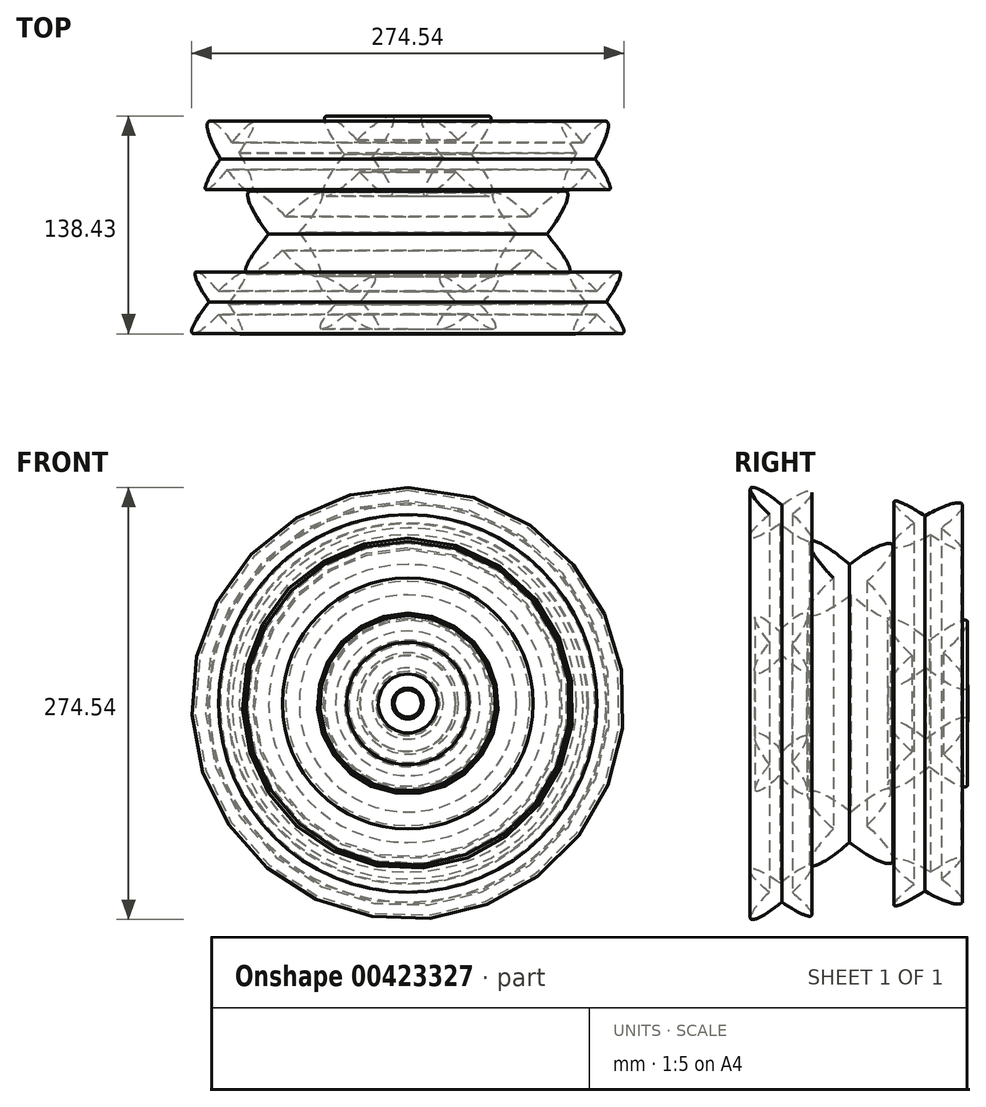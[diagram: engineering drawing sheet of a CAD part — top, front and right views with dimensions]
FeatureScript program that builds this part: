
annotation { "Feature Type Name" : "Feature", "Feature Type Description" : "" }
export const myFeature = defineFeature(function(context is Context, id is Id, definition is map)
    precondition{}
    {
        {
            var Q0;
            Q0=qCreatedBy(makeId("Top.planeOp"),FACE);
            var sketch = newSketch(context, id + "F0", { "sketchPlane" : qUnion([Q0])});
            skEllipticalArc(sketch, "E0", {});
            skEllipticalArc(sketch, "E1", {});
            skEllipticalArc(sketch, "E2.trimOffspring", {});
            skEllipticalArc(sketch, "E3.trimOffspring", {});
            skLineSegment(sketch, "E4", {"start": v(-1.03, 10.72) * mm, "end": v(-9.67, 0.48) * mm});
            skLineSegment(sketch, "E5", {"start": v(1.03, -10.72) * mm, "end": v(9.67, -0.48) * mm});
            skLineSegment(sketch, "E6", {"start": v(-1.03, 10.72) * mm, "end": v(9.67, -0.48) * mm});
            skLineSegment(sketch, "E7", {"start": v(-9.67, 0.48) * mm, "end": v(1.03, -10.72) * mm});
            skEllipse(sketch, "E8", {"center": v(-47.24, 49.23) * mm, "majorRadius": 33.26 * mm, "minorRadius": 7.43 * mm, "majorAxis": v(0.66, -0.75)});
            skEllipse(sketch, "E9", {"center": v(-47.24, 49.23) * mm, "majorRadius": 32.66 * mm, "minorRadius": 6.11 * mm, "majorAxis": v(-0.64, -0.77)});
            skEllipse(sketch, "E10", {"center": v(34.44, 49.23) * mm, "majorRadius": 26.22 * mm, "minorRadius": 3.86 * mm, "majorAxis": v(0.58, -0.81)});
            skEllipse(sketch, "E11", {"center": v(34.44, 49.23) * mm, "majorRadius": 25.72 * mm, "minorRadius": 6.06 * mm, "majorAxis": v(-0.52, -0.85)});
            skEllipse(sketch, "E12", {"center": v(-40.54, -44.04) * mm, "majorRadius": 24.86 * mm, "minorRadius": 5.96 * mm, "majorAxis": v(0.76, 0.65)});
            skEllipse(sketch, "E13", {"center": v(-40.54, -44.04) * mm, "majorRadius": 23.72 * mm, "minorRadius": 4.81 * mm, "majorAxis": v(0.73, -0.68)});
            skEllipse(sketch, "E14", {"center": v(41.45, -44.04) * mm, "majorRadius": 25.5 * mm, "minorRadius": 4.98 * mm, "majorAxis": v(0.66, -0.75)});
            skEllipse(sketch, "E15", {"center": v(41.45, -44.04) * mm, "majorRadius": 24.38 * mm, "minorRadius": 4.5 * mm, "majorAxis": v(-0.6, -0.8)});
            skLineSegment(sketch, "E16", {"start": v(-78.64, 71.48) * mm, "end": v(-78.64, -70.26) * mm});
            const initialGuessF0  = {"E0": [0, 0, -0.6406158775959403, -0.7678615092397738, 0.03473282763399038, 0.007845882429823885, 4.880818733139201, 1.3508733820816232], "E1": [0, 0, 0.6872618986570745, -0.7264097209249565, 0.035036424872981996, 0.006828572059690051, 1.8156771173609703, 4.5113287056147815], "E2.trimOffspring": [0, 0, 0.6872618986570745, -0.7264097209249565, 0.035036424872981996, 0.006828572059690051, 4.957269770950763, 1.3697360520249888], "E3.trimOffspring": [0, 0, -0.6406158775959403, -0.7678615092397738, 0.03473282763399038, 0.007845882429823885, 1.7392260795494074, 4.492466035671416]};
            skSetInitialGuess(sketch, initialGuessF0);
            skSolve(sketch);
        }
        {
            var Q0;
            {var subQ0=sQuery(id+"F0.wireOp",EDGE,"E9");var subQ1=sQuery(id+"F0.wireOp",EDGE,"E8");var subQ2=makeQuery(id+"F0.imprint","INTERSECT",VERTEX,{"disambiguationData":[OD(0.0)],"derivedFrom":[subQ1,subQ0]});Q0=makeQuery(id+"F0.imprint","IMPRINT",FACE,{"disambiguationData":[TD([[makeQuery(id+"F0.imprint","IMPRINT",EDGE,{"disambiguationData":[TD([[subQ2,-1.0]])],"derivedFrom":subQ1}),1.0]])]});}
            var Q1;
            Q1=makeQuery(id+"F0.imprint","IMPRINT",FACE,{"disambiguationData":[TD([[makeQuery(id+"F0.imprint","IMPRINT",EDGE,{"derivedFrom":sQuery(id+"F0.wireOp",EDGE,"E4")}),1.0]])]});
            var Q2;
            {var subQ0=sQuery(id+"F0.wireOp",EDGE,"E15");var subQ1=sQuery(id+"F0.wireOp",EDGE,"E14");var subQ2=makeQuery(id+"F0.imprint","INTERSECT",VERTEX,{"disambiguationData":[OD(2.0)],"derivedFrom":[subQ1,subQ0]});Q2=makeQuery(id+"F0.imprint","IMPRINT",FACE,{"disambiguationData":[TD([[makeQuery(id+"F0.imprint","IMPRINT",EDGE,{"disambiguationData":[TD([[subQ2,-1.0]])],"derivedFrom":subQ1}),-1.0]])]});}
            var Q3;
            {var subQ0=sQuery(id+"F0.wireOp",EDGE,"E9");var subQ1=sQuery(id+"F0.wireOp",EDGE,"E8");var subQ2=makeQuery(id+"F0.imprint","INTERSECT",VERTEX,{"disambiguationData":[OD(0.0)],"derivedFrom":[subQ1,subQ0]});Q3=makeQuery(id+"F0.imprint","IMPRINT",FACE,{"disambiguationData":[TD([[makeQuery(id+"F0.imprint","IMPRINT",EDGE,{"disambiguationData":[TD([[subQ2,1.0]])],"derivedFrom":subQ1}),-1.0]])]});}
            var Q4;
            {var subQ0=sQuery(id+"F0.wireOp",EDGE,"E15");var subQ1=sQuery(id+"F0.wireOp",EDGE,"E14");var subQ2=makeQuery(id+"F0.imprint","INTERSECT",VERTEX,{"disambiguationData":[OD(0.0)],"derivedFrom":[subQ1,subQ0]});Q4=makeQuery(id+"F0.imprint","IMPRINT",FACE,{"disambiguationData":[TD([[makeQuery(id+"F0.imprint","IMPRINT",EDGE,{"disambiguationData":[TD([[subQ2,1.0]])],"derivedFrom":subQ1}),-1.0]])]});}
            var Q5;
            {var subQ0=sQuery(id+"F0.wireOp",EDGE,"E13");var subQ1=sQuery(id+"F0.wireOp",EDGE,"E12");var subQ2=makeQuery(id+"F0.imprint","INTERSECT",VERTEX,{"disambiguationData":[OD(2.0)],"derivedFrom":[subQ1,subQ0]});Q5=makeQuery(id+"F0.imprint","IMPRINT",FACE,{"disambiguationData":[TD([[makeQuery(id+"F0.imprint","IMPRINT",EDGE,{"disambiguationData":[TD([[subQ2,-1.0]])],"derivedFrom":subQ1}),-1.0]])]});}
            var Q6;
            {var subQ0=sQuery(id+"F0.wireOp",EDGE,"E9");var subQ1=sQuery(id+"F0.wireOp",EDGE,"E8");var subQ2=makeQuery(id+"F0.imprint","INTERSECT",VERTEX,{"disambiguationData":[OD(2.0)],"derivedFrom":[subQ1,subQ0]});Q6=makeQuery(id+"F0.imprint","IMPRINT",FACE,{"disambiguationData":[TD([[makeQuery(id+"F0.imprint","IMPRINT",EDGE,{"disambiguationData":[TD([[subQ2,-1.0]])],"derivedFrom":subQ1}),-1.0]])]});}
            var Q7;
            {var subQ0=sQuery(id+"F0.wireOp",EDGE,"E13");var subQ1=sQuery(id+"F0.wireOp",EDGE,"E12");var subQ2=makeQuery(id+"F0.imprint","INTERSECT",VERTEX,{"disambiguationData":[OD(1.0)],"derivedFrom":[subQ1,subQ0]});Q7=makeQuery(id+"F0.imprint","IMPRINT",FACE,{"disambiguationData":[TD([[makeQuery(id+"F0.imprint","IMPRINT",EDGE,{"disambiguationData":[TD([[subQ2,1.0]])],"derivedFrom":subQ1}),1.0]])]});}
            var Q8;
            {var subQ0=sQuery(id+"F0.wireOp",EDGE,"E11");var subQ1=sQuery(id+"F0.wireOp",EDGE,"E10");var subQ2=makeQuery(id+"F0.imprint","INTERSECT",VERTEX,{"disambiguationData":[OD(0.0)],"derivedFrom":[subQ1,subQ0]});Q8=makeQuery(id+"F0.imprint","IMPRINT",FACE,{"disambiguationData":[TD([[makeQuery(id+"F0.imprint","IMPRINT",EDGE,{"disambiguationData":[TD([[subQ2,1.0]])],"derivedFrom":subQ1}),-1.0]])]});}
            var Q9;
            {var subQ0=sQuery(id+"F0.wireOp",EDGE,"E9");var subQ1=sQuery(id+"F0.wireOp",EDGE,"E8");var subQ2=makeQuery(id+"F0.imprint","INTERSECT",VERTEX,{"disambiguationData":[OD(1.0)],"derivedFrom":[subQ1,subQ0]});Q9=makeQuery(id+"F0.imprint","IMPRINT",FACE,{"disambiguationData":[TD([[makeQuery(id+"F0.imprint","IMPRINT",EDGE,{"disambiguationData":[TD([[subQ2,1.0]])],"derivedFrom":subQ1}),1.0]])]});}
            var Q10;
            Q10=makeQuery(id+"F0.imprint","IMPRINT",FACE,{"disambiguationData":[TD([[makeQuery(id+"F0.imprint","IMPRINT",EDGE,{"derivedFrom":sQuery(id+"F0.wireOp",EDGE,"E0")}),1.0]])]});
            var Q11;
            {var subQ0=sQuery(id+"F0.wireOp",EDGE,"E13");var subQ1=sQuery(id+"F0.wireOp",EDGE,"E12");var subQ2=makeQuery(id+"F0.imprint","INTERSECT",VERTEX,{"disambiguationData":[OD(0.0)],"derivedFrom":[subQ1,subQ0]});Q11=makeQuery(id+"F0.imprint","IMPRINT",FACE,{"disambiguationData":[TD([[makeQuery(id+"F0.imprint","IMPRINT",EDGE,{"disambiguationData":[TD([[subQ2,-1.0]])],"derivedFrom":subQ1}),1.0]])]});}
            var Q12;
            Q12=makeQuery(id+"F0.imprint","IMPRINT",FACE,{"disambiguationData":[TD([[makeQuery(id+"F0.imprint","IMPRINT",EDGE,{"derivedFrom":sQuery(id+"F0.wireOp",EDGE,"E3.trimOffspring")}),1.0]])]});
            var Q13;
            Q13=makeQuery(id+"F0.imprint","IMPRINT",FACE,{"disambiguationData":[TD([[makeQuery(id+"F0.imprint","IMPRINT",EDGE,{"derivedFrom":sQuery(id+"F0.wireOp",EDGE,"E1")}),1.0]])]});
            var Q14;
            {var subQ0=sQuery(id+"F0.wireOp",EDGE,"E11");var subQ1=sQuery(id+"F0.wireOp",EDGE,"E10");var subQ2=makeQuery(id+"F0.imprint","INTERSECT",VERTEX,{"disambiguationData":[OD(0.0)],"derivedFrom":[subQ1,subQ0]});Q14=makeQuery(id+"F0.imprint","IMPRINT",FACE,{"disambiguationData":[TD([[makeQuery(id+"F0.imprint","IMPRINT",EDGE,{"disambiguationData":[TD([[subQ2,1.0]])],"derivedFrom":subQ1}),1.0]])]});}
            var Q15;
            Q15=makeQuery(id+"F0.imprint","IMPRINT",FACE,{"disambiguationData":[TD([[makeQuery(id+"F0.imprint","IMPRINT",EDGE,{"derivedFrom":sQuery(id+"F0.wireOp",EDGE,"E2.trimOffspring")}),1.0]])]});
            var Q16;
            {var subQ0=sQuery(id+"F0.wireOp",EDGE,"E15");var subQ1=sQuery(id+"F0.wireOp",EDGE,"E14");var subQ2=makeQuery(id+"F0.imprint","INTERSECT",VERTEX,{"disambiguationData":[OD(0.0)],"derivedFrom":[subQ1,subQ0]});Q16=makeQuery(id+"F0.imprint","IMPRINT",FACE,{"disambiguationData":[TD([[makeQuery(id+"F0.imprint","IMPRINT",EDGE,{"disambiguationData":[TD([[subQ2,1.0]])],"derivedFrom":subQ1}),1.0]])]});}
            var Q17;
            {var subQ0=sQuery(id+"F0.wireOp",EDGE,"E11");var subQ1=sQuery(id+"F0.wireOp",EDGE,"E10");var subQ2=makeQuery(id+"F0.imprint","INTERSECT",VERTEX,{"disambiguationData":[OD(0.0)],"derivedFrom":[subQ1,subQ0]});Q17=makeQuery(id+"F0.imprint","IMPRINT",FACE,{"disambiguationData":[TD([[makeQuery(id+"F0.imprint","IMPRINT",EDGE,{"disambiguationData":[TD([[subQ2,-1.0]])],"derivedFrom":subQ1}),1.0]])]});}
            var Q18;
            {var subQ0=sQuery(id+"F0.wireOp",EDGE,"E11");var subQ1=sQuery(id+"F0.wireOp",EDGE,"E10");var subQ2=makeQuery(id+"F0.imprint","INTERSECT",VERTEX,{"disambiguationData":[OD(2.0)],"derivedFrom":[subQ1,subQ0]});Q18=makeQuery(id+"F0.imprint","IMPRINT",FACE,{"disambiguationData":[TD([[makeQuery(id+"F0.imprint","IMPRINT",EDGE,{"disambiguationData":[TD([[subQ2,-1.0]])],"derivedFrom":subQ1}),-1.0]])]});}
            var Q19;
            {var subQ0=sQuery(id+"F0.wireOp",EDGE,"E11");var subQ1=sQuery(id+"F0.wireOp",EDGE,"E10");var subQ2=makeQuery(id+"F0.imprint","INTERSECT",VERTEX,{"disambiguationData":[OD(1.0)],"derivedFrom":[subQ1,subQ0]});Q19=makeQuery(id+"F0.imprint","IMPRINT",FACE,{"disambiguationData":[TD([[makeQuery(id+"F0.imprint","IMPRINT",EDGE,{"disambiguationData":[TD([[subQ2,1.0]])],"derivedFrom":subQ1}),1.0]])]});}
            var Q20;
            {var subQ0=sQuery(id+"F0.wireOp",EDGE,"E13");var subQ1=sQuery(id+"F0.wireOp",EDGE,"E12");var subQ2=makeQuery(id+"F0.imprint","INTERSECT",VERTEX,{"disambiguationData":[OD(0.0)],"derivedFrom":[subQ1,subQ0]});Q20=makeQuery(id+"F0.imprint","IMPRINT",FACE,{"disambiguationData":[TD([[makeQuery(id+"F0.imprint","IMPRINT",EDGE,{"disambiguationData":[TD([[subQ2,1.0]])],"derivedFrom":subQ1}),-1.0]])]});}
            var Q21;
            {var subQ0=sQuery(id+"F0.wireOp",EDGE,"E15");var subQ1=sQuery(id+"F0.wireOp",EDGE,"E14");var subQ2=makeQuery(id+"F0.imprint","INTERSECT",VERTEX,{"disambiguationData":[OD(0.0)],"derivedFrom":[subQ1,subQ0]});Q21=makeQuery(id+"F0.imprint","IMPRINT",FACE,{"disambiguationData":[TD([[makeQuery(id+"F0.imprint","IMPRINT",EDGE,{"disambiguationData":[TD([[subQ2,-1.0]])],"derivedFrom":subQ1}),1.0]])]});}
            var Q22;
            {var subQ0=sQuery(id+"F0.wireOp",EDGE,"E15");var subQ1=sQuery(id+"F0.wireOp",EDGE,"E14");var subQ2=makeQuery(id+"F0.imprint","INTERSECT",VERTEX,{"disambiguationData":[OD(1.0)],"derivedFrom":[subQ1,subQ0]});Q22=makeQuery(id+"F0.imprint","IMPRINT",FACE,{"disambiguationData":[TD([[makeQuery(id+"F0.imprint","IMPRINT",EDGE,{"disambiguationData":[TD([[subQ2,1.0]])],"derivedFrom":subQ1}),1.0]])]});}
            var Q23;
            {var subQ0=sQuery(id+"F0.wireOp",EDGE,"E9");var subQ1=sQuery(id+"F0.wireOp",EDGE,"E8");var subQ2=makeQuery(id+"F0.imprint","INTERSECT",VERTEX,{"disambiguationData":[OD(0.0)],"derivedFrom":[subQ1,subQ0]});Q23=makeQuery(id+"F0.imprint","IMPRINT",FACE,{"disambiguationData":[TD([[makeQuery(id+"F0.imprint","IMPRINT",EDGE,{"disambiguationData":[TD([[subQ2,1.0]])],"derivedFrom":subQ1}),1.0]])]});}
            var Q24;
            {var subQ0=sQuery(id+"F0.wireOp",EDGE,"E13");var subQ1=sQuery(id+"F0.wireOp",EDGE,"E12");var subQ2=makeQuery(id+"F0.imprint","INTERSECT",VERTEX,{"disambiguationData":[OD(0.0)],"derivedFrom":[subQ1,subQ0]});Q24=makeQuery(id+"F0.imprint","IMPRINT",FACE,{"disambiguationData":[TD([[makeQuery(id+"F0.imprint","IMPRINT",EDGE,{"disambiguationData":[TD([[subQ2,1.0]])],"derivedFrom":subQ1}),1.0]])]});}
            var Q25;
            Q25=sQuery(id+"F0.wireOp",EDGE,"E16");
            revolve(context, id + "F1", {"entities" : qUnion([Q0, Q1, Q2, Q3, Q4, Q5, Q6, Q7, Q8, Q9, Q10, Q11, Q12, Q13, Q14, Q15, Q16, Q17, Q18, Q19, Q20, Q21, Q22, Q23, Q24]), "axis" : qUnion([Q25]), "revolveType" : RevolveType.FULL});
        }
    });
